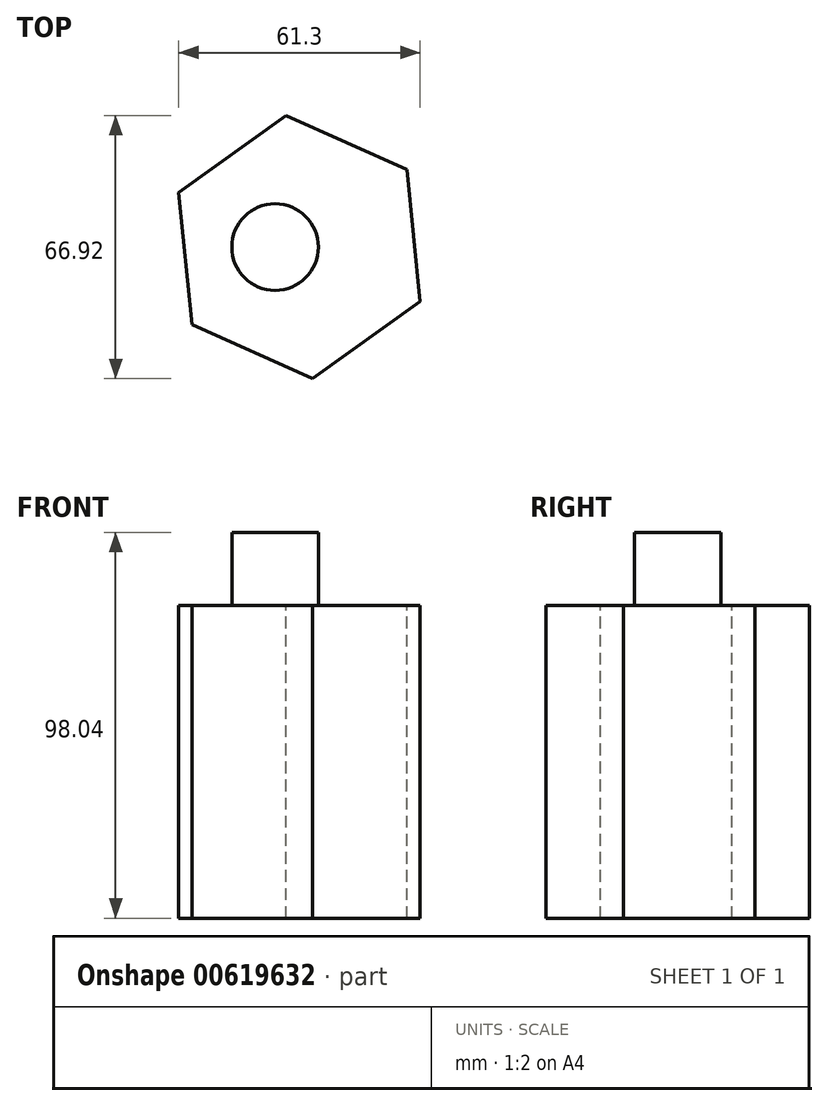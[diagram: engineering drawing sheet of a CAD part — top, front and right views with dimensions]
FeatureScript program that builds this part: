
annotation { "Feature Type Name" : "Feature", "Feature Type Description" : "" }
export const myFeature = defineFeature(function(context is Context, id is Id, definition is map)
    precondition{}
    {
        {
            var Q0;
            Q0=qCreatedBy(makeId("Top.planeOp"),FACE);
            var sketch = newSketch(context, id + "F0", { "sketchPlane" : qUnion([Q0])});
            skCircle(sketch, "E0.cCircle", {"center": v(0, 0) * mm, "radius": 29.12 * mm, "construction": true});
            skLineSegment(sketch, "E0.0", {"start": v(-30.65, 13.83) * mm, "end": v(-3.35, 33.46) * mm});
            skLineSegment(sketch, "E0.1", {"start": v(-3.35, 33.46) * mm, "end": v(27.3, 19.63) * mm});
            skLineSegment(sketch, "E0.2", {"start": v(27.3, 19.63) * mm, "end": v(30.65, -13.83) * mm});
            skLineSegment(sketch, "E0.3", {"start": v(30.65, -13.83) * mm, "end": v(3.35, -33.46) * mm});
            skLineSegment(sketch, "E0.4", {"start": v(3.35, -33.46) * mm, "end": v(-27.3, -19.63) * mm});
            skLineSegment(sketch, "E0.5", {"start": v(-27.3, -19.63) * mm, "end": v(-30.65, 13.83) * mm});
            skPoint(sketch, "E0.0.midPoint", {"position": v(-17, 23.65) * mm});
            skSolve(sketch);
        }
        {
            var Q0;
            Q0=makeQuery(id+"F0.imprint","IMPRINT",FACE,{"disambiguationData":[TD([[makeQuery(id+"F0.imprint","IMPRINT",EDGE,{"derivedFrom":sQuery(id+"F0.wireOp",EDGE,"E0.0")}),-1.0]])]});
            extrude(context, id + "F1", {"entities" : qUnion([Q0]), "oppositeDirection" : true, "depth" : 79.5 * mm, "offsetDistance" : 25.4 * mm});
        }
        {
            var Q0;
            Q0=qCreatedBy(makeId("Top.planeOp"),FACE);
            var sketch = newSketch(context, id + "F2", { "sketchPlane" : qUnion([Q0])});
            skCircle(sketch, "E1", {"center": v(-6.18, 0) * mm, "radius": 11 * mm});
            skSolve(sketch);
        }
        {
            var Q0;
            Q0=makeQuery(id+"F2.imprint","IMPRINT",FACE,{"disambiguationData":[TD([[makeQuery(id+"F2.imprint","IMPRINT",EDGE,{"derivedFrom":sQuery(id+"F2.wireOp",EDGE,"E1")}),1.0]])]});
            extrude(context, id + "F3", {"entities" : qUnion([Q0]), "operationType" : NewBodyOperationType.ADD, "depth" : 18.54 * mm, "offsetDistance" : 25.4 * mm});
        }
    });
